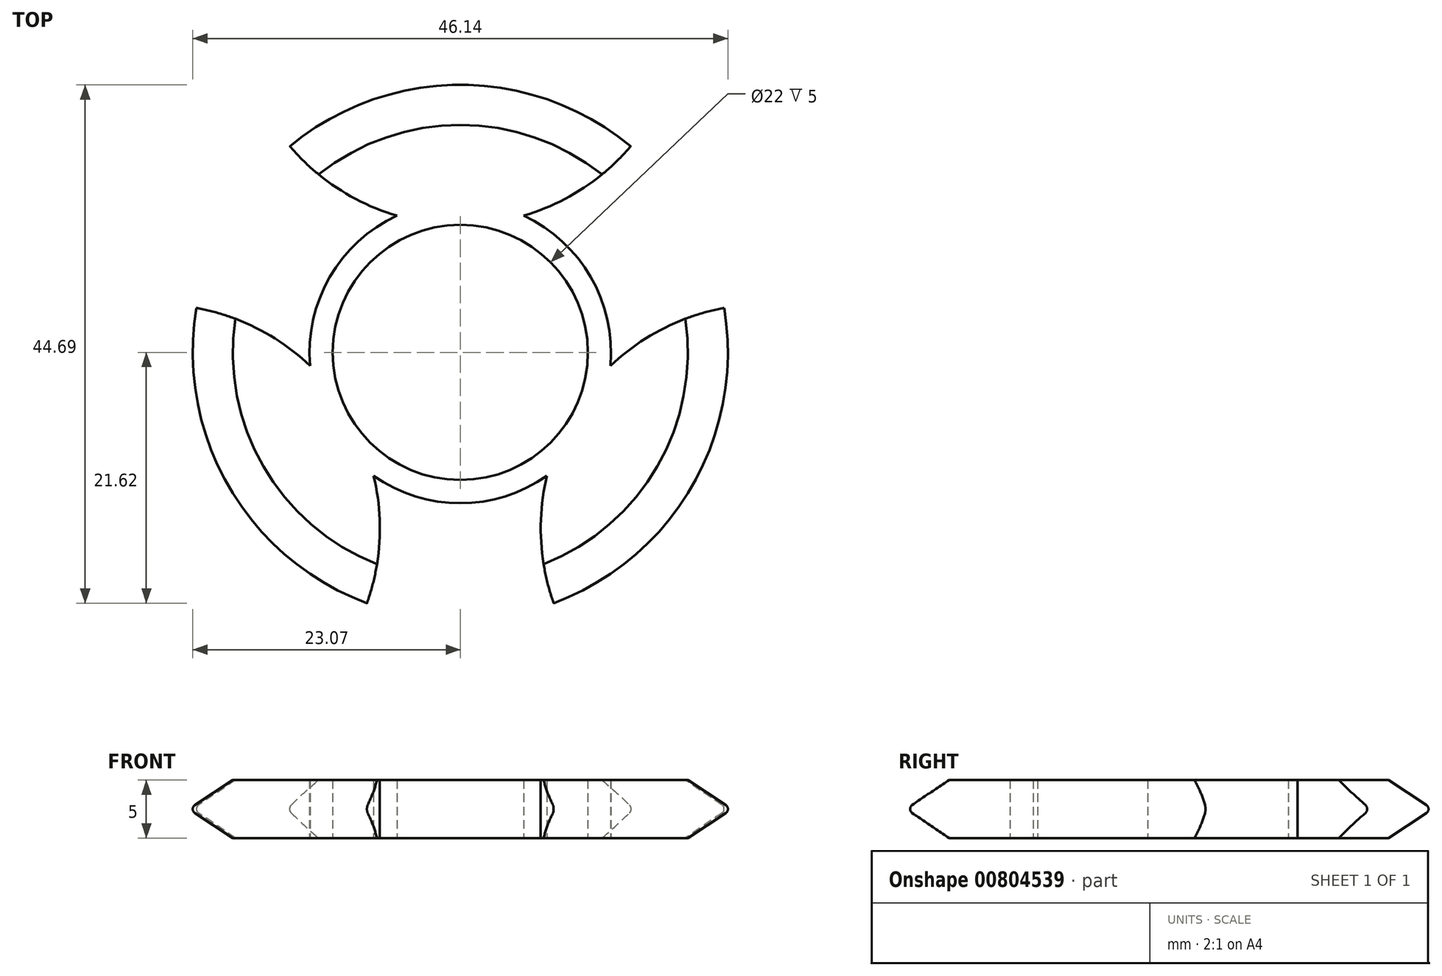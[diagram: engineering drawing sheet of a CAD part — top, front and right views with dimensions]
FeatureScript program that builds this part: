
annotation { "Feature Type Name" : "Feature", "Feature Type Description" : "" }
export const myFeature = defineFeature(function(context is Context, id is Id, definition is map)
    precondition{}
    {
        {
            var Q0;
            Q0=qCreatedBy(makeId("Top.planeOp"),FACE);
            var sketch = newSketch(context, id + "F0", { "sketchPlane" : qUnion([Q0])});
            skCircle(sketch, "E0", {"center": v(0, 0) * mm, "radius": 11 * mm, "construction": true});
            skCircle(sketch, "E1.cCircle", {"center": v(0, 30.32) * mm, "radius": 15 * mm, "construction": true});
            skLineSegment(sketch, "E1.0", {"start": v(15, 21.66) * mm, "end": v(0, 13) * mm, "construction": true});
            skLineSegment(sketch, "E1.1", {"start": v(0, 13) * mm, "end": v(-15, 21.66) * mm, "construction": true});
            skLineSegment(sketch, "E1.2", {"start": v(-15, 21.66) * mm, "end": v(-15, 38.98) * mm, "construction": true});
            skLineSegment(sketch, "E1.3", {"start": v(-15, 38.98) * mm, "end": v(0, 47.64) * mm, "construction": true});
            skLineSegment(sketch, "E1.4", {"start": v(0, 47.64) * mm, "end": v(15, 38.98) * mm, "construction": true});
            skLineSegment(sketch, "E1.5", {"start": v(15, 38.98) * mm, "end": v(15, 21.66) * mm, "construction": true});
            skPoint(sketch, "E1.0.midPoint", {"position": v(7.5, 17.33) * mm});
            skCircle(sketch, "E2.1.0", {"center": v(-26.26, -15.16) * mm, "radius": 15 * mm, "construction": true});
            skLineSegment(sketch, "E2.1.1", {"start": v(-41.26, -6.5) * mm, "end": v(-26.26, 2.16) * mm, "construction": true});
            skLineSegment(sketch, "E2.1.2", {"start": v(-41.26, -23.82) * mm, "end": v(-41.26, -6.5) * mm, "construction": true});
            skLineSegment(sketch, "E2.1.4", {"start": v(-11.26, -6.5) * mm, "end": v(-11.26, -23.82) * mm, "construction": true});
            skPoint(sketch, "E2.1.5", {"position": v(-18.76, -2.17) * mm});
            skLineSegment(sketch, "E2.1.6", {"start": v(-26.26, 2.16) * mm, "end": v(-11.26, -6.5) * mm, "construction": true});
            skLineSegment(sketch, "E2.1.7", {"start": v(-26.26, -32.48) * mm, "end": v(-41.26, -23.82) * mm, "construction": true});
            skLineSegment(sketch, "E2.1.8", {"start": v(-11.26, -23.82) * mm, "end": v(-26.26, -32.48) * mm, "construction": true});
            skCircle(sketch, "E2.2.0", {"center": v(26.26, -15.16) * mm, "radius": 15 * mm, "construction": true});
            skLineSegment(sketch, "E2.2.1", {"start": v(26.26, -32.48) * mm, "end": v(11.26, -23.82) * mm, "construction": true});
            skLineSegment(sketch, "E2.2.2", {"start": v(41.26, -23.82) * mm, "end": v(26.26, -32.48) * mm, "construction": true});
            skLineSegment(sketch, "E2.2.4", {"start": v(11.26, -6.5) * mm, "end": v(26.26, 2.16) * mm, "construction": true});
            skPoint(sketch, "E2.2.5", {"position": v(11.26, -15.16) * mm});
            skLineSegment(sketch, "E2.2.6", {"start": v(11.26, -23.82) * mm, "end": v(11.26, -6.5) * mm, "construction": true});
            skLineSegment(sketch, "E2.2.7", {"start": v(41.26, -6.5) * mm, "end": v(41.26, -23.82) * mm, "construction": true});
            skLineSegment(sketch, "E2.2.8", {"start": v(26.26, 2.16) * mm, "end": v(41.26, -6.5) * mm, "construction": true});
            skArc(sketch, "E3", {"start": v(5.47, 11.8) * mm, "mid": v(0, 13) * mm, "end": v(-5.47, 11.8) * mm, "construction": true});
            skArc(sketch, "E4", {"start": v(-5.47, 11.8) * mm, "mid": v(-11.26, 6.5) * mm, "end": v(-12.95, -1.16) * mm});
            skArc(sketch, "E5", {"start": v(-12.95, -1.16) * mm, "mid": v(-11.26, -6.5) * mm, "end": v(-7.48, -10.64) * mm, "construction": true});
            skArc(sketch, "E6", {"start": v(-7.48, -10.64) * mm, "mid": v(0, -13) * mm, "end": v(7.48, -10.64) * mm});
            skArc(sketch, "E7", {"start": v(7.48, -10.64) * mm, "mid": v(11.26, -6.5) * mm, "end": v(12.95, -1.16) * mm, "construction": true});
            skArc(sketch, "E8", {"start": v(12.95, -1.16) * mm, "mid": v(11.26, 6.5) * mm, "end": v(5.47, 11.8) * mm});
            skArc(sketch, "E9", {"start": v(12.95, -1.16) * mm, "mid": v(9.53, -5.5) * mm, "end": v(7.48, -10.64) * mm, "construction": true});
            skArc(sketch, "E10", {"start": v(7.48, -10.64) * mm, "mid": v(43, -24.82) * mm, "end": v(12.95, -1.16) * mm});
            skArc(sketch, "E11", {"start": v(-7.48, -10.64) * mm, "mid": v(-9.53, -5.5) * mm, "end": v(-12.95, -1.16) * mm, "construction": true});
            skArc(sketch, "E12", {"start": v(-12.95, -1.16) * mm, "mid": v(-43, -24.82) * mm, "end": v(-7.48, -10.64) * mm});
            skArc(sketch, "E13", {"start": v(-5.47, 11.8) * mm, "mid": v(0, 11) * mm, "end": v(5.47, 11.8) * mm, "construction": true});
            skArc(sketch, "E14", {"start": v(5.47, 11.8) * mm, "mid": v(0, 49.64) * mm, "end": v(-5.47, 11.8) * mm});
            skSolve(sketch);
        }
        {
            var Q0;
            Q0 = qSketchRegion(id + "F0", true);
            extrude(context, id + "F1", {"entities" : qUnion([Q0]), "depth" : 5 * mm, "offsetDistance" : 25 * mm});
        }
        {
            var Q0;
            Q0=makeQuery(id+"F1.opExtrude","CAP_FACE",FACE,{"disambiguationData":[OSD([sQuery(id+"F0.wireOp",EDGE,"E4"),sQuery(id+"F0.wireOp",EDGE,"E6"),sQuery(id+"F0.wireOp",EDGE,"E8"),sQuery(id+"F0.wireOp",EDGE,"E10"),sQuery(id+"F0.wireOp",EDGE,"E12"),sQuery(id+"F0.wireOp",EDGE,"E14")])],"isStart":true});
            var sketch = newSketch(context, id + "F2", { "sketchPlane" : qUnion([Q0])});
            skLineSegment(sketch, "E15.0", {"start": v(26.26, -2.16) * mm, "end": v(41.26, 6.5) * mm, "construction": true});
            skLineSegment(sketch, "E15.1", {"start": v(41.26, 6.5) * mm, "end": v(41.26, 23.82) * mm, "construction": true});
            skLineSegment(sketch, "E15.2", {"start": v(41.26, 23.82) * mm, "end": v(26.26, 32.48) * mm, "construction": true});
            skLineSegment(sketch, "E15.3", {"start": v(26.26, 32.48) * mm, "end": v(11.26, 23.82) * mm, "construction": true});
            skLineSegment(sketch, "E15.4", {"start": v(11.26, 23.82) * mm, "end": v(11.26, 6.5) * mm, "construction": true});
            skLineSegment(sketch, "E15.5", {"start": v(11.26, 6.5) * mm, "end": v(26.26, -2.16) * mm, "construction": true});
            skLineSegment(sketch, "E15.6", {"start": v(15, -38.98) * mm, "end": v(15, -21.66) * mm, "construction": true});
            skLineSegment(sketch, "E15.7", {"start": v(15, -21.66) * mm, "end": v(0, -13) * mm, "construction": true});
            skLineSegment(sketch, "E15.8", {"start": v(0, -13) * mm, "end": v(-15, -21.66) * mm, "construction": true});
            skLineSegment(sketch, "E15.9", {"start": v(-15, -21.66) * mm, "end": v(-15, -38.98) * mm, "construction": true});
            skLineSegment(sketch, "E15.10", {"start": v(-15, -38.98) * mm, "end": v(0, -47.64) * mm, "construction": true});
            skLineSegment(sketch, "E15.11", {"start": v(0, -47.64) * mm, "end": v(15, -38.98) * mm, "construction": true});
            skLineSegment(sketch, "E15.12", {"start": v(-41.26, 6.5) * mm, "end": v(-26.26, -2.16) * mm, "construction": true});
            skLineSegment(sketch, "E15.13", {"start": v(-41.26, 23.82) * mm, "end": v(-41.26, 6.5) * mm, "construction": true});
            skLineSegment(sketch, "E15.14", {"start": v(-26.26, 32.48) * mm, "end": v(-41.26, 23.82) * mm, "construction": true});
            skLineSegment(sketch, "E15.15", {"start": v(-11.26, 23.82) * mm, "end": v(-26.26, 32.48) * mm, "construction": true});
            skLineSegment(sketch, "E15.16", {"start": v(-11.26, 6.5) * mm, "end": v(-11.26, 23.82) * mm, "construction": true});
            skLineSegment(sketch, "E15.17", {"start": v(-26.26, -2.16) * mm, "end": v(-11.26, 6.5) * mm, "construction": true});
            skCircle(sketch, "E16.0", {"center": v(0, 0) * mm, "radius": 11 * mm});
            skSolve(sketch);
        }
        {
            var Q0;
            Q0 = qSketchRegion(id + "F2", true);
            extrude(context, id + "F3", {"entities" : qUnion([Q0]), "operationType" : NewBodyOperationType.REMOVE, "oppositeDirection" : true, "depth" : 25 * mm, "offsetDistance" : 25 * mm});
        }
        {
            var Q0;
            Q0=makeQuery(id+"F1.opExtrude","CAP_FACE",FACE,{"disambiguationData":[OSD([sQuery(id+"F0.wireOp",EDGE,"E4"),sQuery(id+"F0.wireOp",EDGE,"E6"),sQuery(id+"F0.wireOp",EDGE,"E8"),sQuery(id+"F0.wireOp",EDGE,"E10"),sQuery(id+"F0.wireOp",EDGE,"E12"),sQuery(id+"F0.wireOp",EDGE,"E14")])],"isStart":false});
            var sketch = newSketch(context, id + "F4", { "sketchPlane" : qUnion([Q0])});
            skCircle(sketch, "E17", {"center": v(0, 0) * mm, "radius": 23.4 * mm});
            skSolve(sketch);
        }
        {
            var Q0;
            Q0 = qSketchRegion(id + "F4", true);
            extrude(context, id + "F5", {"entities" : qUnion([Q0]), "operationType" : NewBodyOperationType.INTERSECT, "oppositeDirection" : true, "depth" : 25 * mm, "offsetDistance" : 25 * mm});
        }
        {
            var Q0;
            Q0=qCreatedBy(makeId("Right.planeOp"),FACE);
            var sketch = newSketch(context, id + "F6", { "sketchPlane" : qUnion([Q0])});
            skLineSegment(sketch, "E18.0.0", {"start": v(19.62, 0) * mm, "end": v(19.62, 5) * mm, "construction": true});
            skLineSegment(sketch, "E18.0.1", {"start": v(19.62, 5) * mm, "end": v(23.4, 5) * mm});
            skLineSegment(sketch, "E18.0.2", {"start": v(18.04, 5) * mm, "end": v(18.04, 0) * mm, "construction": true});
            skLineSegment(sketch, "E18.0.3", {"start": v(19.62, 0) * mm, "end": v(23.4, 0) * mm});
            skLineSegment(sketch, "E19", {"start": v(22.9, 2.84) * mm, "end": v(19.62, 5) * mm});
            skLineSegment(sketch, "E20", {"start": v(22.9, 2.16) * mm, "end": v(19.62, 0) * mm});
            skLineSegment(sketch, "E21", {"start": v(23.4, 5) * mm, "end": v(23.4, 0) * mm});
            skLineSegment(sketch, "E22", {"start": v(0, 0) * mm, "end": v(0, 41.23) * mm, "construction": true});
            skPoint(sketch, "E23.visualSharp", {"position": v(23.4, 2.5) * mm});
            skArc(sketch, "E23.filletArc", {"start": v(22.9, 2.16) * mm, "mid": v(23.07, 2.5) * mm, "end": v(22.9, 2.84) * mm});
            skSolve(sketch);
        }
        {
            var Q0;
            {var subQ0=sQuery(id+"F6.wireOp",EDGE,"E18.0.3");Q0=makeQuery(id+"F6.imprint","IMPRINT",FACE,{"disambiguationData":[TD([[makeQuery(id+"F6.imprint","IMPRINT",EDGE,{"derivedFrom":subQ0}),1.0]])]});}
            var Q1;
            {var subQ0=sQuery(id+"F6.wireOp",EDGE,"E18.0.1");Q1=makeQuery(id+"F6.imprint","IMPRINT",FACE,{"disambiguationData":[TD([[makeQuery(id+"F6.imprint","IMPRINT",EDGE,{"derivedFrom":subQ0}),-1.0]])]});}
            var Q2;
            Q2=sQuery(id+"F6.wireOp",EDGE,"E19");
            var Q3;
            Q3=sQuery(id+"F6.wireOp",EDGE,"E18.0.1");
            var Q4;
            Q4=sQuery(id+"F6.wireOp",EDGE,"E21");
            var Q5;
            Q5=sQuery(id+"F6.wireOp",EDGE,"E20");
            var Q6;
            Q6=sQuery(id+"F6.wireOp",EDGE,"E18.0.3");
            var Q7;
            Q7=sQuery(id+"F6.wireOp",EDGE,"E22");
            revolve(context, id + "F7", {"operationType" : NewBodyOperationType.REMOVE, "surfaceOperationType" : NewSurfaceOperationType.NEW, "entities" : qUnion([Q0, Q1]), "surfaceEntities" : qUnion([Q2, Q3, Q4, Q5, Q6]), "axis" : qUnion([Q7]), "revolveType" : RevolveType.FULL});
        }
    });
